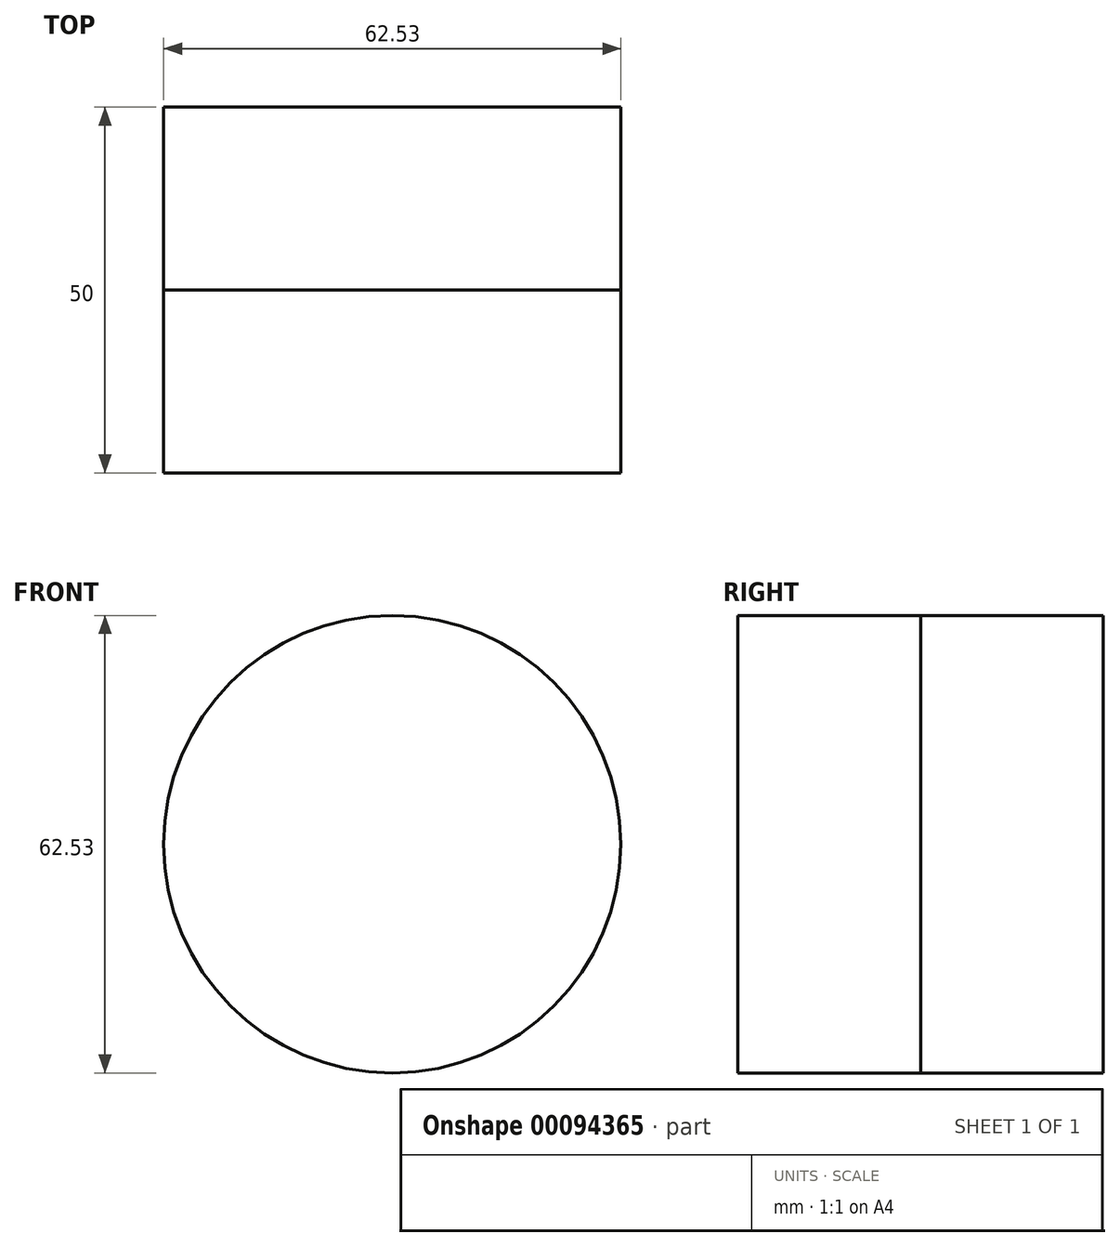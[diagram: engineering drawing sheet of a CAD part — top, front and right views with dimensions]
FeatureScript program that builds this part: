
annotation { "Feature Type Name" : "Feature", "Feature Type Description" : "" }
export const myFeature = defineFeature(function(context is Context, id is Id, definition is map)
    precondition{}
    {
        {
            var Q0;
            Q0=qCreatedBy(makeId("Front.planeOp"),FACE);
            var sketch = newSketch(context, id + "F0", { "sketchPlane" : qUnion([Q0])});
            skCircle(sketch, "E0", {"center": v(0.57, -0.1) * mm, "radius": 31.27 * mm});
            skSolve(sketch);
        }
        {
            var Q0;
            Q0=makeQuery(id+"F0.imprint","IMPRINT",FACE,{"disambiguationData":[TD([[makeQuery(id+"F0.imprint","IMPRINT",EDGE,{"derivedFrom":sQuery(id+"F0.wireOp",EDGE,"E0")}),1.0]])]});
            var Q1;
            Q1=sQuery(id+"F0.wireOp",EDGE,"E0");
            extrude(context, id + "F1", {"entities" : qUnion([Q0]), "surfaceEntities" : qUnion([Q1]), "depth" : 25 * mm});
        }
        {
            var Q0;
            Q0=makeQuery(id+"F1.opExtrude","SWEPT_BODY",BODY,{"disambiguationData":[OSD([sQuery(id+"F0.wireOp",EDGE,"E0")])]});
            var Q1;
            Q1=qCreatedBy(makeId("Front.planeOp"),FACE);
            mirror(context, id + "F2", {"entities" : qUnion([Q0]), "mirrorPlane" : qUnion([Q1])});
        }
    });
